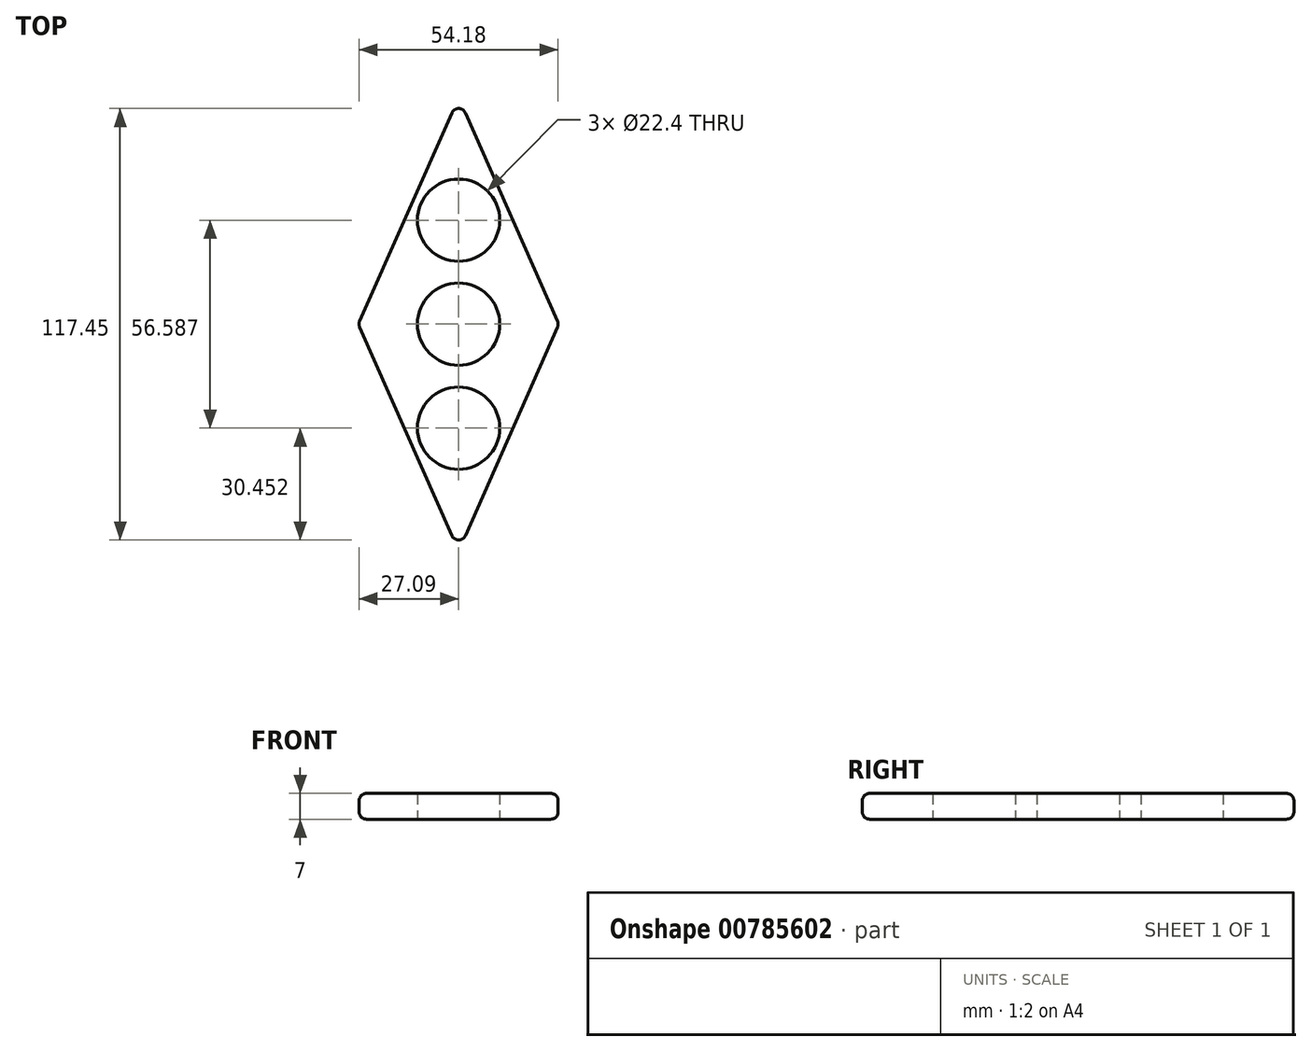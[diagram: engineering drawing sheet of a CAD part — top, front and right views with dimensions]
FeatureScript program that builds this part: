
annotation { "Feature Type Name" : "Feature", "Feature Type Description" : "" }
export const myFeature = defineFeature(function(context is Context, id is Id, definition is map)
    precondition{}
    {
        {
            var Q0;
            Q0=qCreatedBy(makeId("Top.planeOp"),FACE);
            var sketch = newSketch(context, id + "F0", { "sketchPlane" : qUnion([Q0])});
            skCircle(sketch, "E0", {"center": v(0, 0) * mm, "radius": 11.2 * mm});
            skCircle(sketch, "E1", {"center": v(0, 28.27) * mm, "radius": 11.2 * mm});
            skCircle(sketch, "E2", {"center": v(0, -28.32) * mm, "radius": 11.2 * mm});
            skLineSegment(sketch, "E3", {"start": v(0, 61.62) * mm, "end": v(-27.28, 0) * mm});
            skLineSegment(sketch, "E4", {"start": v(-27.28, 0) * mm, "end": v(0, -61.71) * mm});
            skLineSegment(sketch, "E5", {"start": v(0, -61.71) * mm, "end": v(27.28, 0) * mm});
            skLineSegment(sketch, "E6", {"start": v(27.28, 0) * mm, "end": v(0, 61.62) * mm});
            skSolve(sketch);
        }
        {
            var Q0;
            Q0=makeQuery(id+"F0.imprint","IMPRINT",FACE,{"disambiguationData":[TD([[makeQuery(id+"F0.imprint","IMPRINT",EDGE,{"derivedFrom":sQuery(id+"F0.wireOp",EDGE,"E0")}),-1.0]])]});
            extrude(context, id + "F1", {"entities" : qUnion([Q0]), "depth" : 7 * mm, "offsetDistance" : 25 * mm});
        }
        {
            var Q0;
            Q0=makeQuery(id+"F1.opExtrude","SWEPT_FACE",FACE,{"disambiguationData":[OSD([sQuery(id+"F0.wireOp",EDGE,"E6")])]});
            var Q1;
            Q1=makeQuery(id+"F1.opExtrude","CAP_EDGE",EDGE,{"disambiguationData":[OSD([sQuery(id+"F0.wireOp",EDGE,"E5")])],"isStart":false});
            var Q2;
            Q2=makeQuery(id+"F1.opExtrude","SWEPT_FACE",FACE,{"disambiguationData":[OSD([sQuery(id+"F0.wireOp",EDGE,"E3")])]});
            var Q3;
            Q3=makeQuery(id+"F1.opExtrude","SWEPT_FACE",FACE,{"disambiguationData":[OSD([sQuery(id+"F0.wireOp",EDGE,"E4")])]});
            var Q4;
            Q4=makeQuery(id+"F1.opExtrude","CAP_EDGE",EDGE,{"disambiguationData":[OSD([sQuery(id+"F0.wireOp",EDGE,"E5")])],"isStart":true});
            fillet(context, id + "F2", {"entities" : qUnion([Q0, Q1, Q2, Q3, Q4]), "radius" : 2 * mm, "tangentPropagation" : true, "allowEdgeOverflow" : false});
        }
    });
